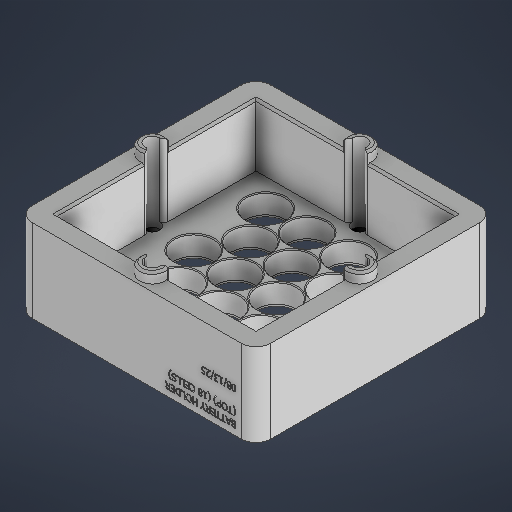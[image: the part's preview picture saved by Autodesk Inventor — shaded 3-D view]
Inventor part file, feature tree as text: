
AUTODESK INVENTOR PART (.ipt)
format: ipt  version: 2025 (Build 290162000, 162)  size: 1,054,720 bytes
history: native  units: in
note: dims shown in document units (in); Inventor stores cm internally (conversion verified against a paired STEP export)
features: sketch x8, extrude x4, hole x2, fillet x2, chamfer x2
ambient origin geometry x8: Origin, YZ Plane, XZ Plane, XY Plane, X Axis, Y Axis, Z Axis, Center Point
bodies: Solid1 (feature_tree)
feature tree (18):
  extrude  "Extrusion1"  Depth=4.5276in
  sketch  "Sketch4"  dims[d2=0.3937in d3=0.0in d48=3.7795in]
  extrude  "Extrusion3"  Depth=3.7795in
  hole  "Hole4"  [1 undecoded]
  hole  "Hole5"  [1 undecoded]
  extrude  "Extrusion4"  Depth=1.5748in
  fillet  "Fillet1"  Radius=0.748in
  fillet  "Fillet2"  Radius=0.3937in
  chamfer  "Chamfer1"  Distance=1.1811in
  chamfer  "Chamfer2"  Distance=3.937in
  extrude  "Extrusion5"  Depth=3.937in
  sketch  "Sketch1"  dims[d0=4.5276in d1=4.5276in]
  sketch  "Sketch Rectangular Pattern11"  dims[d147=0.6819in]
  sketch  "Sketch Rectangular Pattern12"  dims[d148=1.1811in d150=0.7874in d151=0.7874in d153=1.3638in d174=1.1811in d175=0.0in]
  sketch  "Sketch6"  dims[d49=3.7795in d124=1.3638in]
  sketch  "Sketch Rectangular Pattern14"  dims[d176=0.7323in d177=0.2362in d178=0.748in d179=0.0787in d180=0.0172in d181=0.315in d182=0.8108in d183=3.937in d184=3.937in d185=0.2362in d186=1.1811in d188=1.9685in d189=1.1811in d191=1.9685in d194=0.2805in d195=0.2362in d196=0.5118in d197=0.2756in d198=0.0172in d199=0.315in d200=0.8108in d201=0.4724in d202=0.4724in d203=0.4724in d204=0.4724in d205=0.1969in d206=0.0in d207=0.2805in d208=0.0787in d209=0.0157in d210=0.0787in d211=45.0deg d212=0.0394in d213=0.0787in d214=45.0deg d215=0.0787in d216=0.0in]
  sketch  "Sketch7"  dims[d132=2.3622in d133=2.7276in]
  sketch  "Sketch8"  dims[d134=0.748in d135=1.5748in d137=0.7874in d138=1.1811in d140=1.3638in d143=0.748in d146=0.3937in]
note: 2 required parameter values undecoded (feature->parameter linkage not recoverable at this tier; creation-order binding heuristic only, values carry confidence <= 0.55)
